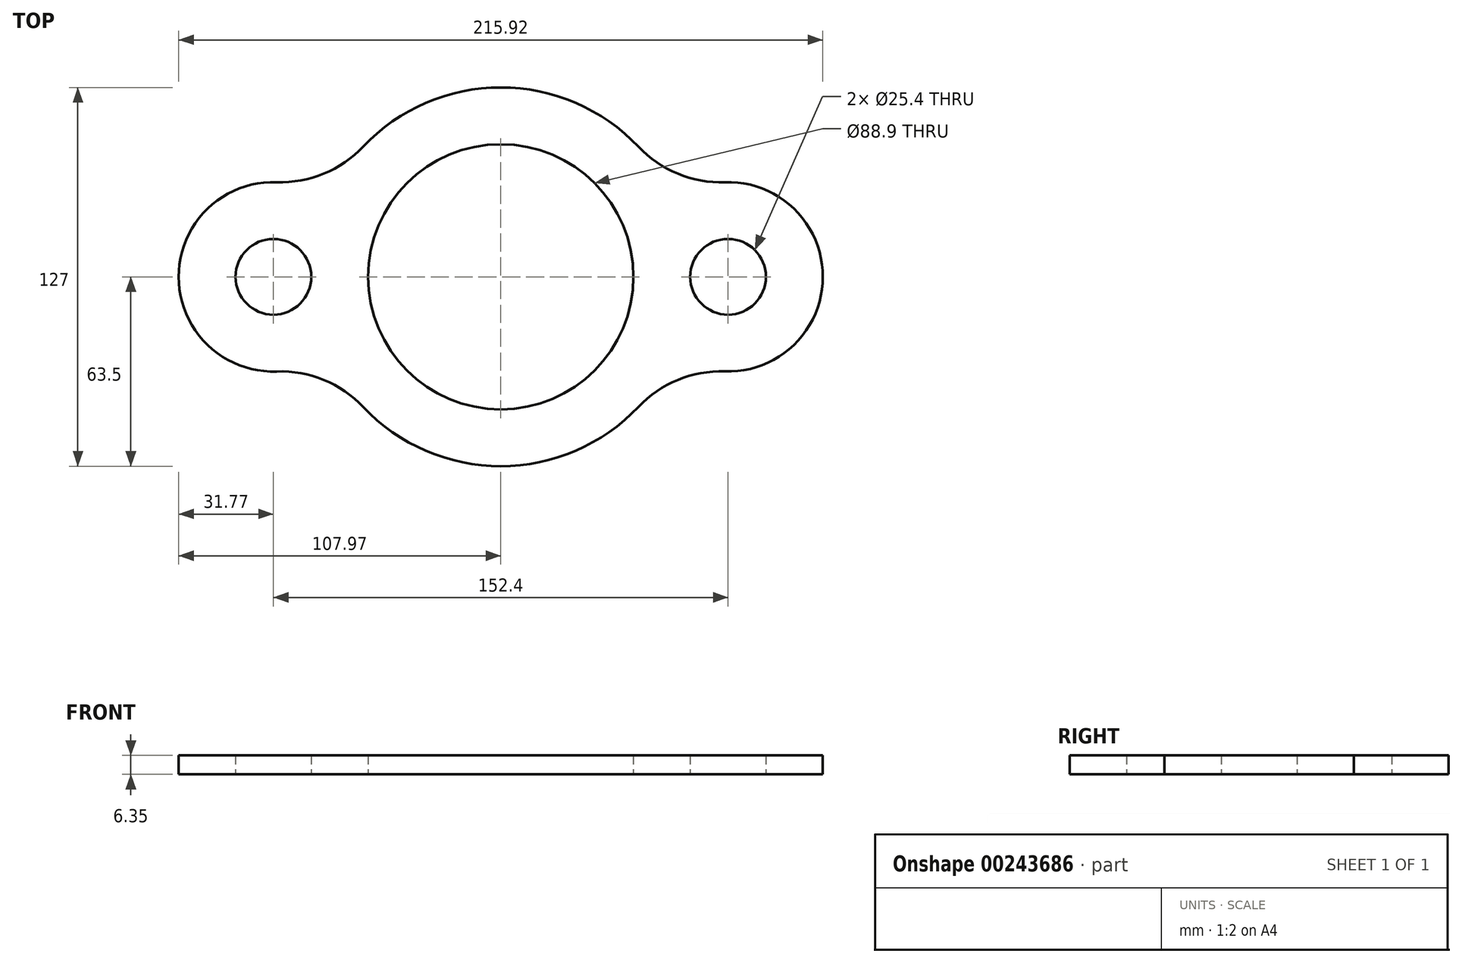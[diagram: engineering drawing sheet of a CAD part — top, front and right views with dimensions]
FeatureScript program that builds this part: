
annotation { "Feature Type Name" : "Feature", "Feature Type Description" : "" }
export const myFeature = defineFeature(function(context is Context, id is Id, definition is map)
    precondition{}
    {
        {
            var Q0;
            Q0=qCreatedBy(makeId("Top.planeOp"),FACE);
            var sketch = newSketch(context, id + "F0", { "sketchPlane" : qUnion([Q0])});
            skArc(sketch, "E0", {"start": v(-46.13, -43.64) * mm, "mid": v(0, -63.5) * mm, "end": v(46.14, -43.63) * mm});
            skCircle(sketch, "E1", {"center": v(0, 0) * mm, "radius": 44.45 * mm});
            skArc(sketch, "E2", {"start": v(75.12, -31.73) * mm, "mid": v(107.95, 0) * mm, "end": v(75.12, 31.73) * mm});
            skArc(sketch, "E3", {"start": v(-75.1, 31.75) * mm, "mid": v(-107.97, 0) * mm, "end": v(-75.1, -31.75) * mm});
            skArc(sketch, "E4.trimOffspring", {"start": v(46.14, 43.63) * mm, "mid": v(0, 63.5) * mm, "end": v(-46.13, 43.64) * mm});
            skCircle(sketch, "E5", {"center": v(-76.2, 0) * mm, "radius": 12.7 * mm});
            skCircle(sketch, "E6", {"center": v(76.2, 0) * mm, "radius": 12.7 * mm});
            skPoint(sketch, "E7.visualSharp", {"position": v(-57.94, 26) * mm});
            skArc(sketch, "E7.filletArc", {"start": v(-75.1, 31.75) * mm, "mid": v(-59.34, 34.58) * mm, "end": v(-46.13, 43.64) * mm});
            skPoint(sketch, "E8.visualSharp", {"position": v(57.94, 25.98) * mm});
            skArc(sketch, "E8.filletArc", {"start": v(46.14, 43.63) * mm, "mid": v(59.35, 34.56) * mm, "end": v(75.12, 31.73) * mm});
            skPoint(sketch, "E9.visualSharp", {"position": v(57.94, -25.98) * mm});
            skArc(sketch, "E9.filletArc", {"start": v(75.12, -31.73) * mm, "mid": v(59.35, -34.56) * mm, "end": v(46.14, -43.63) * mm});
            skPoint(sketch, "E10.visualSharp", {"position": v(-57.94, -26) * mm});
            skArc(sketch, "E10.filletArc", {"start": v(-46.13, -43.64) * mm, "mid": v(-59.34, -34.58) * mm, "end": v(-75.1, -31.75) * mm});
            skLineSegment(sketch, "E11", {"start": v(-76.2, 0) * mm, "end": v(76.2, 0) * mm});
            skSolve(sketch);
        }
        {
            var Q0;
            Q0=makeQuery(id+"F0.imprint","IMPRINT",FACE,{"disambiguationData":[TD([[makeQuery(id+"F0.imprint","IMPRINT",EDGE,{"derivedFrom":sQuery(id+"F0.wireOp",EDGE,"E0")}),1.0]])]});
            extrude(context, id + "F1", {"entities" : qUnion([Q0]), "depth" : 6.35 * mm});
        }
    });
